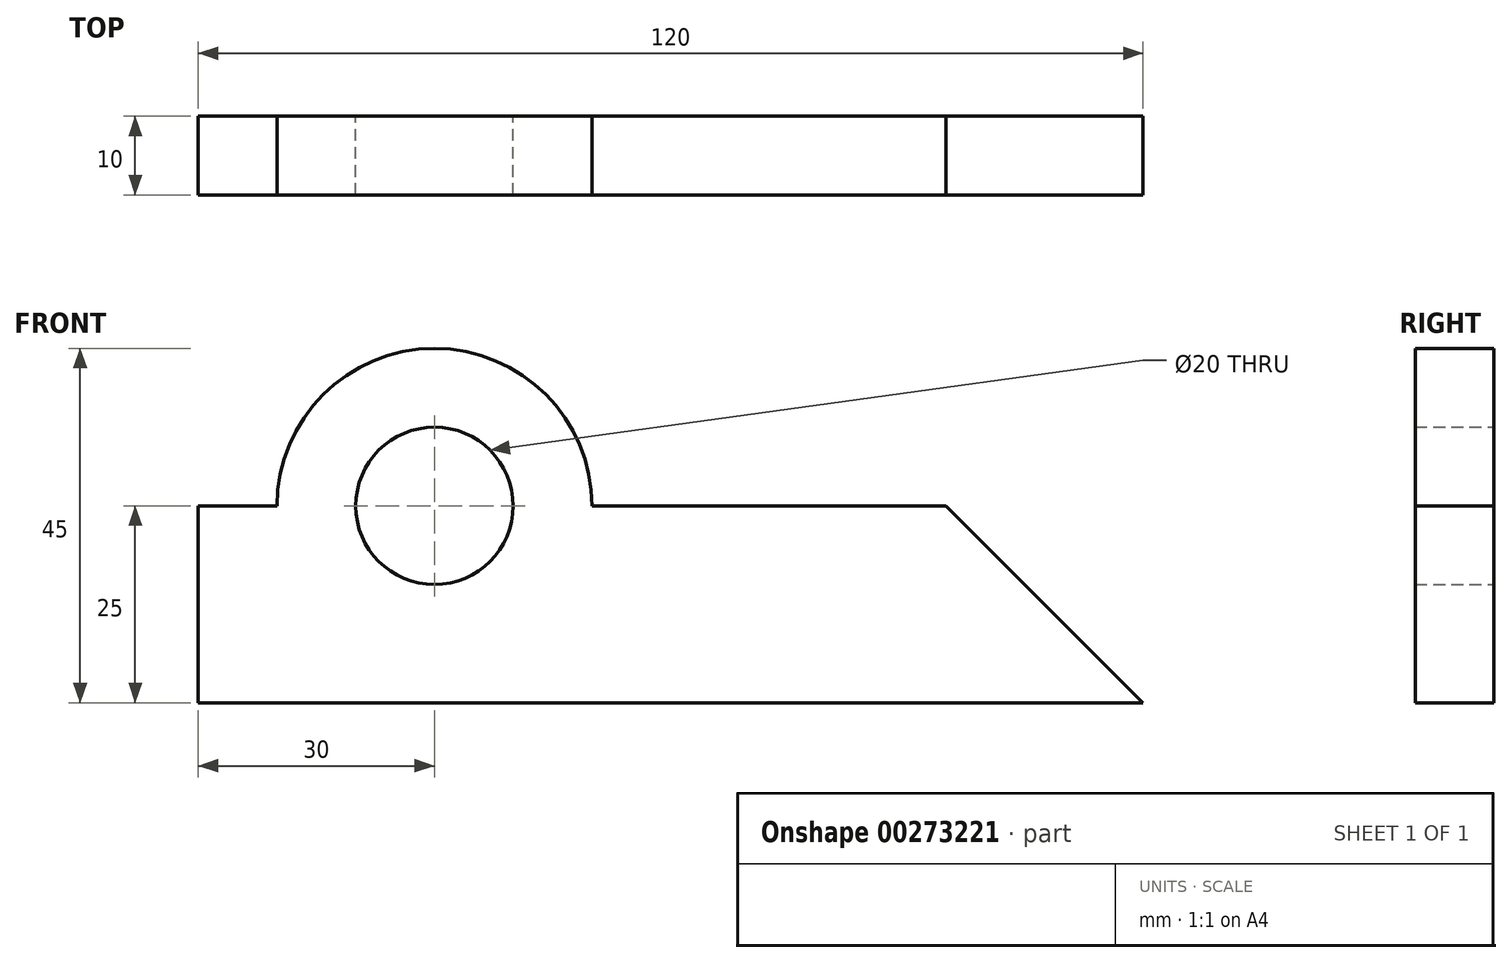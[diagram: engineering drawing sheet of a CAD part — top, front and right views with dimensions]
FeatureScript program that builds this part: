
annotation { "Feature Type Name" : "Feature", "Feature Type Description" : "" }
export const myFeature = defineFeature(function(context is Context, id is Id, definition is map)
    precondition{}
    {
        {
            var Q0;
            Q0=qCreatedBy(makeId("Front.planeOp"),FACE);
            var sketch = newSketch(context, id + "F0", { "sketchPlane" : qUnion([Q0])});
            skLineSegment(sketch, "E0", {"start": v(0, 0) * mm, "end": v(0, 25) * mm});
            skLineSegment(sketch, "E1", {"start": v(0, 0) * mm, "end": v(120, 0) * mm});
            skLineSegment(sketch, "E2", {"start": v(50, 25) * mm, "end": v(95, 25) * mm});
            skLineSegment(sketch, "E3", {"start": v(95, 25) * mm, "end": v(120, 0) * mm});
            skLineSegment(sketch, "E4", {"start": v(0, 25) * mm, "end": v(10, 25) * mm});
            skCircle(sketch, "E5", {"center": v(30, 25) * mm, "radius": 10 * mm});
            skArc(sketch, "E6", {"start": v(50, 25) * mm, "mid": v(30, 45) * mm, "end": v(10, 25) * mm});
            skSolve(sketch);
        }
        {
            var Q0;
            Q0 = qSketchRegion(id + "F0", true);
            extrude(context, id + "F1", {"entities" : qUnion([Q0]), "depth" : 10 * mm});
        }
    });
